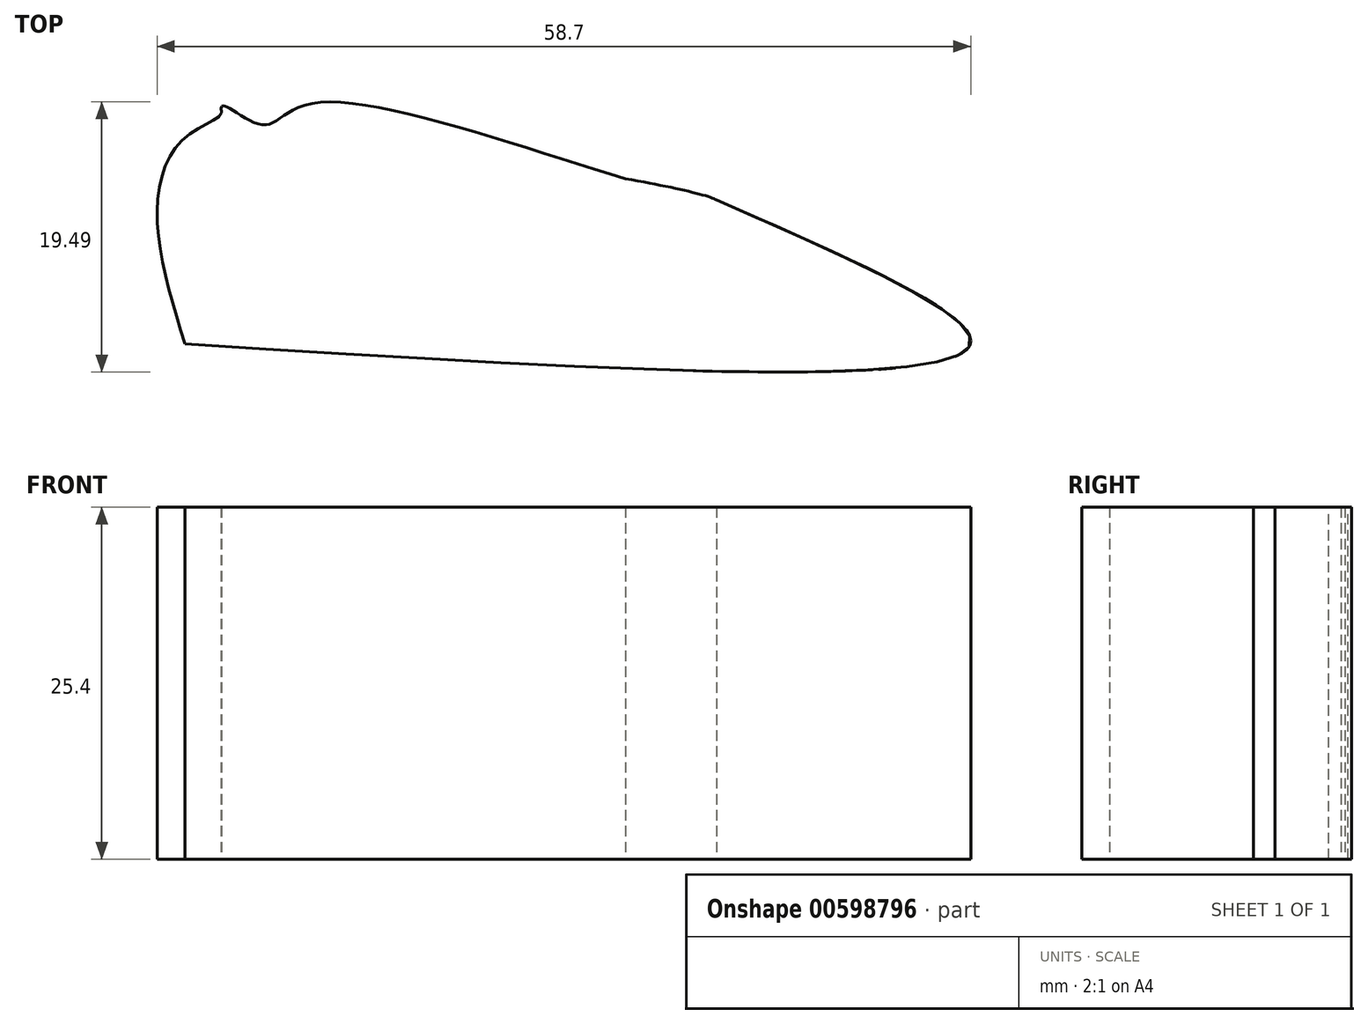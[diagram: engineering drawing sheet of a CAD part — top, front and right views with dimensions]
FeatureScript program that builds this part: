
annotation { "Feature Type Name" : "Feature", "Feature Type Description" : "" }
export const myFeature = defineFeature(function(context is Context, id is Id, definition is map)
    precondition{}
    {
        {
            var Q0;
            Q0=qCreatedBy(makeId("Top.planeOp"),FACE);
            var sketch = newSketch(context, id + "F0", { "sketchPlane" : qUnion([Q0])});
            skFitSpline(sketch, "E0", {"points": [v(-56.7, 0) * mm, v(-58.68, 9.38) * mm, v(-56.7, 14.85) * mm, v(-54.03, 16.68) * mm, v(-54.86, 17.84) * mm], "startDerivative": vector(-8.2, 26.72) * mm, "endDerivative": vector(-10, 8.63) * mm});
            skFitSpline(sketch, "E1", {"points": [v(-54.03, 16.68) * mm, v(-54.03, 17.12) * mm, v(-53.7, 17.12) * mm, v(-51, 15.8) * mm, v(-46.83, 17.44) * mm, v(-17.48, 10.4) * mm, v(-16.78, 11.87) * mm], "startDerivative": vector(-1.41, 9.44) * mm, "endDerivative": vector(-1.48, 18.13) * mm});
            skFitSpline(sketch, "E2", {"points": [v(-18.33, 10.37) * mm, v(0, 0) * mm, v(-56.7, 0) * mm], "startDerivative": vector(74.85, -32.6) * mm, "endDerivative": vector(-134.63, 8.46) * mm});
            skFitSpline(sketch, "E3", {"points": [v(-48.5, 17.05) * mm, v(-47.98, 17.05) * mm, v(-47.77, 16.6) * mm, v(-18.33, 10.37) * mm, v(-18.33, 10.05) * mm], "startDerivative": vector(7.26, 1.12) * mm, "endDerivative": vector(-3.4, -3.94) * mm});
            skLineSegment(sketch, "E4", {"start": v(-54.03, 16.68) * mm, "end": v(-54.04, 16.67) * mm});
            skSolve(sketch);
        }
        {
            var Q0;
            Q0 = qSketchRegion(id + "F0", true);
            extrude(context, id + "F1", {"entities" : qUnion([Q0]), "depth" : 25.4 * mm, "offsetDistance" : 25.4 * mm});
        }
    });
